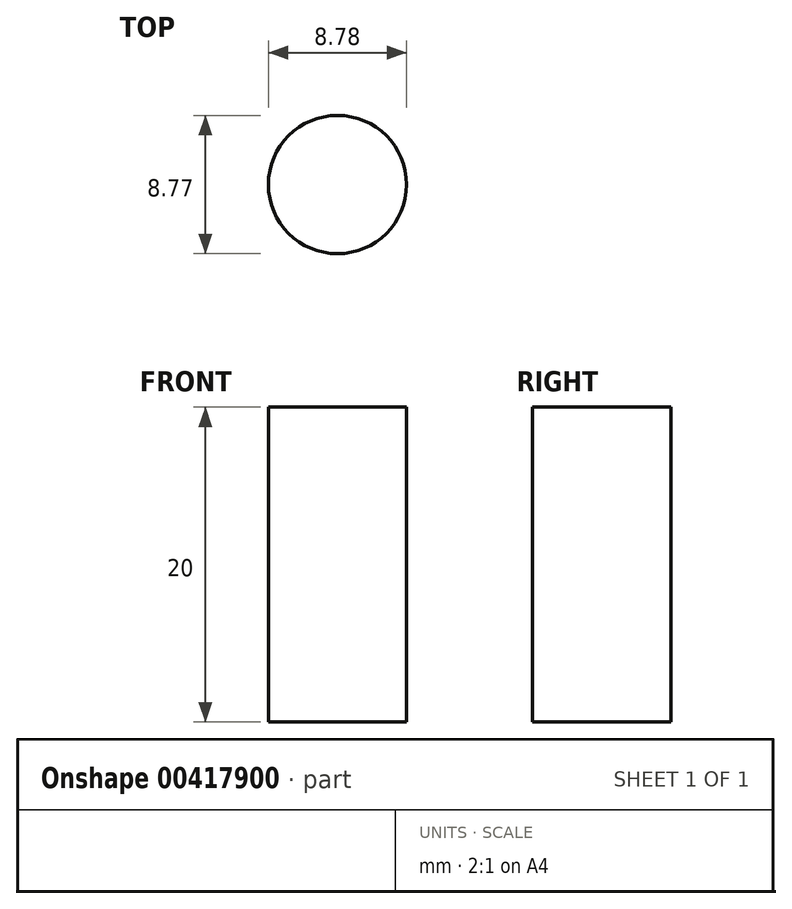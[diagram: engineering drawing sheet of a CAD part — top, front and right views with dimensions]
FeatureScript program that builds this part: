
annotation { "Feature Type Name" : "Feature", "Feature Type Description" : "" }
export const myFeature = defineFeature(function(context is Context, id is Id, definition is map)
    precondition{}
    {
        {
            var Q0;
            Q0=qCreatedBy(makeId("Top.planeOp"),FACE);
            var sketch = newSketch(context, id + "F0", { "sketchPlane" : qUnion([Q0])});
            skCircle(sketch, "E0", {"center": v(-49.13, 49.03) * mm, "radius": 4.39 * mm});
            skSolve(sketch);
        }
        {
            var Q0;
            Q0=makeQuery(id+"F0.imprint","IMPRINT",FACE,{"disambiguationData":[TD([[makeQuery(id+"F0.imprint","IMPRINT",EDGE,{"derivedFrom":sQuery(id+"F0.wireOp",EDGE,"E0")}),1.0]])]});
            extrude(context, id + "F1", {"entities" : qUnion([Q0]), "depth" : 20 * mm});
        }
    });
